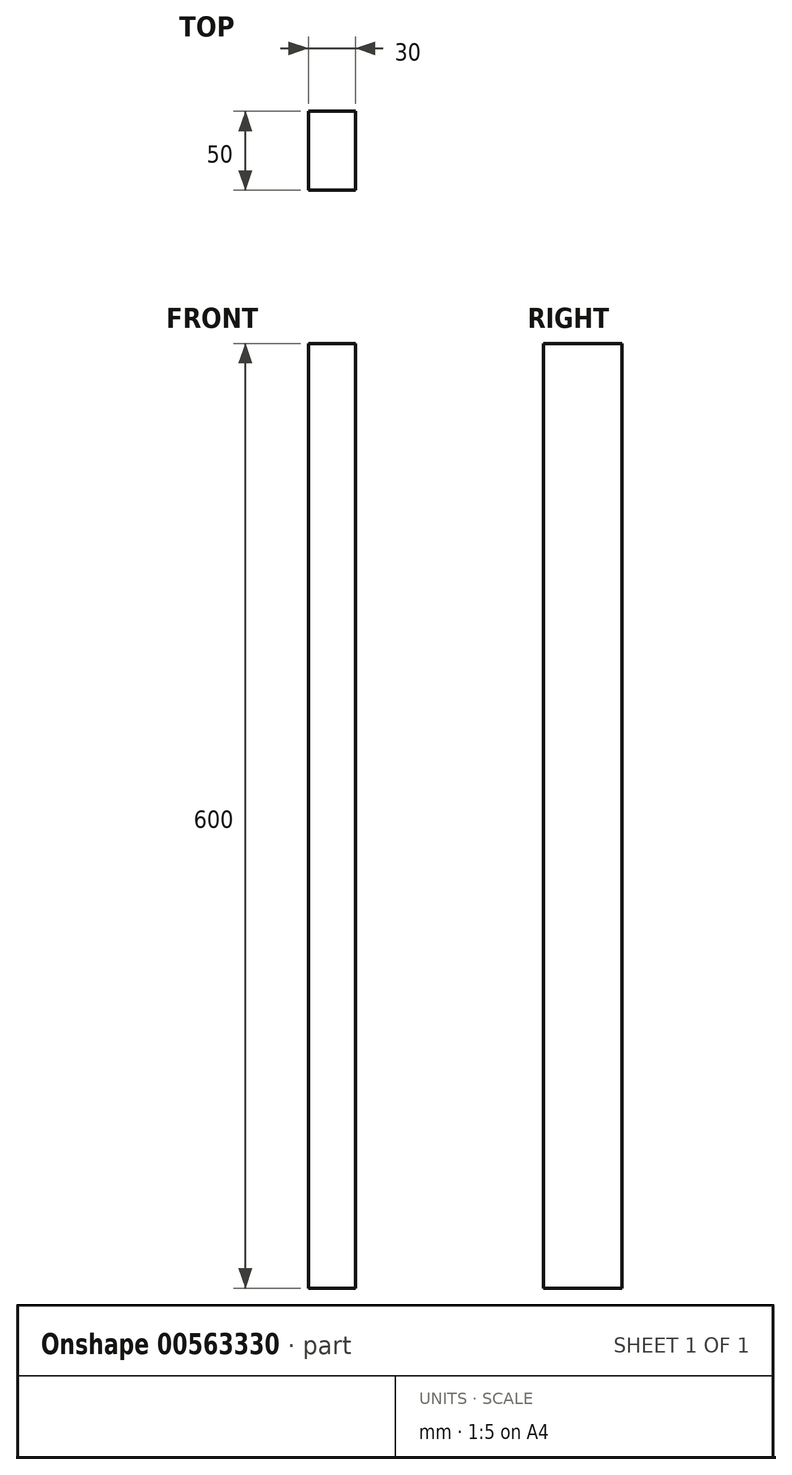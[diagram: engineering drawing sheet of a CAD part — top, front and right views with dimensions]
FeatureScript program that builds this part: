
annotation { "Feature Type Name" : "Feature", "Feature Type Description" : "" }
export const myFeature = defineFeature(function(context is Context, id is Id, definition is map)
    precondition{}
    {
        {
            var Q0;
            Q0=qCreatedBy(makeId("Top.planeOp"),FACE);
            var sketch = newSketch(context, id + "F0", { "sketchPlane" : qUnion([Q0])});
            skLineSegment(sketch, "E0.bottom", {"start": v(0, 0) * mm, "end": v(100, 0) * mm});
            skLineSegment(sketch, "E0.top", {"start": v(0, 100) * mm, "end": v(100, 100) * mm});
            skLineSegment(sketch, "E0.left", {"start": v(0, 0) * mm, "end": v(0, 100) * mm});
            skLineSegment(sketch, "E0.right", {"start": v(100, 0) * mm, "end": v(100, 100) * mm});
            skLineSegment(sketch, "E1.bottom", {"start": v(50, 100) * mm, "end": v(0, 100) * mm});
            skLineSegment(sketch, "E1.top", {"start": v(50, 70) * mm, "end": v(0, 70) * mm});
            skLineSegment(sketch, "E1.left", {"start": v(50, 100) * mm, "end": v(50, 70) * mm});
            skLineSegment(sketch, "E1.right", {"start": v(0, 100) * mm, "end": v(0, 70) * mm});
            skLineSegment(sketch, "E2.bottom", {"start": v(100, 0) * mm, "end": v(70, 0) * mm});
            skLineSegment(sketch, "E2.top", {"start": v(100, 50) * mm, "end": v(70, 50) * mm});
            skLineSegment(sketch, "E2.left", {"start": v(100, 0) * mm, "end": v(100, 50) * mm});
            skLineSegment(sketch, "E2.right", {"start": v(70, 0) * mm, "end": v(70, 50) * mm});
            skSolve(sketch);
        }
        {
            var Q0;
            Q0=makeQuery(id+"F0.imprint","IMPRINT",FACE,{"disambiguationData":[TD([[makeQuery(id+"F0.imprint","IMPRINT",EDGE,{"derivedFrom":sQuery(id+"F0.wireOp",EDGE,"E0.bottom")}),1.0]])]});
            var Q1;
            Q1=sQuery(id+"F0.wireOp",EDGE,"E0.bottom");
            var Q2;
            Q2=sQuery(id+"F0.wireOp",EDGE,"E0.right");
            var Q3;
            Q3=sQuery(id+"F0.wireOp",EDGE,"E0.top");
            var Q4;
            Q4=sQuery(id+"F0.wireOp",EDGE,"E0.left");
            extrude(context, id + "F1", {"entities" : qUnion([Q0]), "surfaceEntities" : qUnion([Q1, Q2, Q3, Q4]), "depth" : 600 * mm, "offsetDistance" : 25.4 * mm});
        }
        {
            var Q0;
            Q0=makeQuery(id+"F1.opExtrude","SWEPT_BODY",BODY,{"disambiguationData":[OSD([sQuery(id+"F0.wireOp",EDGE,"E0.bottom"),sQuery(id+"F0.wireOp",EDGE,"E0.top"),sQuery(id+"F0.wireOp",EDGE,"E0.left"),sQuery(id+"F0.wireOp",EDGE,"E0.right"),sQuery(id+"F0.wireOp",EDGE,"E1.top"),sQuery(id+"F0.wireOp",EDGE,"E1.left"),sQuery(id+"F0.wireOp",EDGE,"E2.top"),sQuery(id+"F0.wireOp",EDGE,"E2.right")])]});
            transform(context, id + "F2", {"entities" : qUnion([Q0]), "transformType" : TransformType.TRANSLATION_3D, "dx" : 0 * mm, "dy" : 0 * mm, "dz" : 0 * mm, "makeCopy" : true});
        }
        {
            var Q0;
            Q0=makeQuery(id+"F2.opPattern","COPY",BODY,{"derivedFrom":makeQuery(id+"F1.opExtrude","SWEPT_BODY",BODY,{"disambiguationData":[OSD([sQuery(id+"F0.wireOp",EDGE,"E0.bottom"),sQuery(id+"F0.wireOp",EDGE,"E0.top"),sQuery(id+"F0.wireOp",EDGE,"E0.left"),sQuery(id+"F0.wireOp",EDGE,"E0.right"),sQuery(id+"F0.wireOp",EDGE,"E1.top"),sQuery(id+"F0.wireOp",EDGE,"E1.left"),sQuery(id+"F0.wireOp",EDGE,"E2.top"),sQuery(id+"F0.wireOp",EDGE,"E2.right")])]}),"instanceName":"1"});
            deleteBodies(context, id + "F3", {"entities" : qUnion([Q0])});
        }
    });
